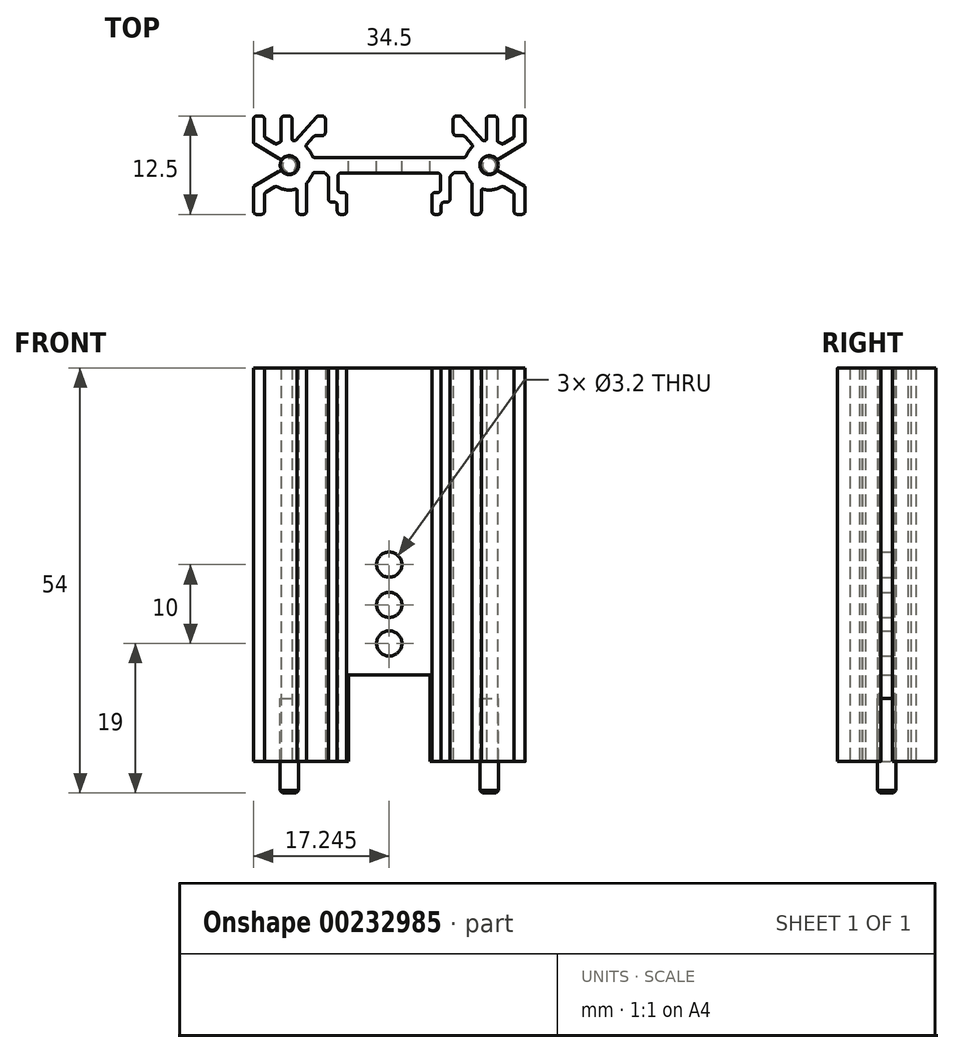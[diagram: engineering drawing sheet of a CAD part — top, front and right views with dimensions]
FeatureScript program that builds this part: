
annotation { "Feature Type Name" : "Feature", "Feature Type Description" : "" }
export const myFeature = defineFeature(function(context is Context, id is Id, definition is map)
    precondition{}
    {
        {
            var Q0;
            Q0=qCreatedBy(makeId("Top.planeOp"),FACE);
            var sketch = newSketch(context, id + "F0", { "sketchPlane" : qUnion([Q0])});
            skArc(sketch, "E0", {"start": v(-11.86, 14.65) * mm, "mid": v(-9.81, 15.5) * mm, "end": v(-11.85, 16.37) * mm});
            skPoint(sketch, "E0.first.point", {"position": v(-10.8, 16.69) * mm});
            skPoint(sketch, "E0.second.point", {"position": v(-9.82, 15.45) * mm});
            skPoint(sketch, "E0.third.point", {"position": v(-10.9, 14.31) * mm});
            skArc(sketch, "E1", {"start": v(-10.41, 18.6) * mm, "mid": v(-10.45, 18.6) * mm, "end": v(-10.48, 18.62) * mm});
            skPoint(sketch, "E1.first.point", {"position": v(-12.46, 18.31) * mm});
            skPoint(sketch, "E1.second.point", {"position": v(-10.9, 12.36) * mm});
            skPoint(sketch, "E1.third.point", {"position": v(-8.35, 17.19) * mm});
            skLineSegment(sketch, "E2", {"start": v(-12.05, 18.63) * mm, "end": v(-12.05, 21.36) * mm});
            skLineSegment(sketch, "E3", {"start": v(-10.65, 21.36) * mm, "end": v(-10.65, 18.81) * mm});
            skLineSegment(sketch, "E4", {"start": v(-10.22, 18.66) * mm, "end": v(-7.56, 21.63) * mm});
            skLineSegment(sketch, "E5", {"start": v(-11.05, 21.76) * mm, "end": v(-11.65, 21.76) * mm});
            skPoint(sketch, "E6.visualSharp", {"position": v(-12.05, 21.76) * mm});
            skArc(sketch, "E6.filletArc", {"start": v(-11.65, 21.76) * mm, "mid": v(-11.93, 21.64) * mm, "end": v(-12.05, 21.36) * mm});
            skPoint(sketch, "E7.visualSharp", {"position": v(-10.65, 21.76) * mm});
            skArc(sketch, "E7.filletArc", {"start": v(-10.65, 21.36) * mm, "mid": v(-10.77, 21.64) * mm, "end": v(-11.05, 21.76) * mm});
            skLineSegment(sketch, "E8", {"start": v(-12.8, 18.24) * mm, "end": v(-14.07, 19) * mm});
            skLineSegment(sketch, "E9", {"start": v(-14.16, 19.17) * mm, "end": v(-14.16, 21.36) * mm});
            skLineSegment(sketch, "E10", {"start": v(-14.56, 21.76) * mm, "end": v(-15.16, 21.76) * mm});
            skLineSegment(sketch, "E11", {"start": v(-15.56, 21.36) * mm, "end": v(-15.56, 18.5) * mm});
            skLineSegment(sketch, "E12", {"start": v(-15.37, 18.16) * mm, "end": v(-13.7, 17.15) * mm});
            skPoint(sketch, "E13.visualSharp", {"position": v(-15.56, 18.28) * mm});
            skArc(sketch, "E13.filletArc", {"start": v(-15.56, 18.5) * mm, "mid": v(-15.51, 18.3) * mm, "end": v(-15.37, 18.16) * mm});
            skPoint(sketch, "E14.visualSharp", {"position": v(-14.16, 19.06) * mm});
            skArc(sketch, "E14.filletArc", {"start": v(-14.16, 19.17) * mm, "mid": v(-14.14, 19.08) * mm, "end": v(-14.07, 19) * mm});
            skPoint(sketch, "E15.visualSharp", {"position": v(-14.16, 21.76) * mm});
            skArc(sketch, "E15.filletArc", {"start": v(-14.16, 21.36) * mm, "mid": v(-14.28, 21.64) * mm, "end": v(-14.56, 21.76) * mm});
            skPoint(sketch, "E16.visualSharp", {"position": v(-15.56, 21.76) * mm});
            skArc(sketch, "E16.filletArc", {"start": v(-15.16, 21.76) * mm, "mid": v(-15.45, 21.64) * mm, "end": v(-15.56, 21.36) * mm});
            skLineSegment(sketch, "E17", {"start": v(-7.92, 19.13) * mm, "end": v(-8.86, 18.08) * mm});
            skLineSegment(sketch, "E18", {"start": v(-13.72, 13.88) * mm, "end": v(-15.47, 12.83) * mm});
            skLineSegment(sketch, "E19", {"start": v(-15.56, 12.66) * mm, "end": v(-15.56, 9.66) * mm});
            skLineSegment(sketch, "E20", {"start": v(-15.16, 9.26) * mm, "end": v(-14.56, 9.26) * mm});
            skLineSegment(sketch, "E21", {"start": v(-14.16, 9.66) * mm, "end": v(-14.16, 11.74) * mm});
            skLineSegment(sketch, "E22", {"start": v(-13.97, 12.09) * mm, "end": v(-12.8, 12.79) * mm});
            skPoint(sketch, "E23.visualSharp", {"position": v(-14.16, 11.97) * mm});
            skArc(sketch, "E23.filletArc", {"start": v(-13.97, 12.09) * mm, "mid": v(-14.11, 11.94) * mm, "end": v(-14.16, 11.74) * mm});
            skPoint(sketch, "E24.visualSharp", {"position": v(-15.56, 12.77) * mm});
            skArc(sketch, "E24.filletArc", {"start": v(-15.47, 12.83) * mm, "mid": v(-15.54, 12.76) * mm, "end": v(-15.56, 12.66) * mm});
            skPoint(sketch, "E25.visualSharp", {"position": v(-14.16, 9.26) * mm});
            skArc(sketch, "E25.filletArc", {"start": v(-14.56, 9.26) * mm, "mid": v(-14.28, 9.38) * mm, "end": v(-14.16, 9.66) * mm});
            skPoint(sketch, "E26.visualSharp", {"position": v(-15.56, 9.26) * mm});
            skArc(sketch, "E26.filletArc", {"start": v(-15.56, 9.66) * mm, "mid": v(-15.45, 9.38) * mm, "end": v(-15.16, 9.26) * mm});
            skLineSegment(sketch, "E27", {"start": v(-10, 12.26) * mm, "end": v(-10, 9.66) * mm});
            skLineSegment(sketch, "E28", {"start": v(-9.6, 9.26) * mm, "end": v(-9.2, 9.26) * mm});
            skLineSegment(sketch, "E29", {"start": v(-8.8, 9.66) * mm, "end": v(-8.8, 13.18) * mm});
            skPoint(sketch, "E30.visualSharp", {"position": v(-10, 9.26) * mm});
            skArc(sketch, "E30.filletArc", {"start": v(-10, 9.66) * mm, "mid": v(-9.88, 9.38) * mm, "end": v(-9.6, 9.26) * mm});
            skPoint(sketch, "E31.visualSharp", {"position": v(-8.8, 9.26) * mm});
            skArc(sketch, "E31.filletArc", {"start": v(-9.2, 9.26) * mm, "mid": v(-8.92, 9.38) * mm, "end": v(-8.8, 9.66) * mm});
            skLineSegment(sketch, "E32", {"start": v(-7.87, 14.55) * mm, "end": v(-6.62, 14.55) * mm});
            skLineSegment(sketch, "E33", {"start": v(-6.48, 14.49) * mm, "end": v(-6.1, 14.1) * mm});
            skLineSegment(sketch, "E34", {"start": v(-6.04, 13.96) * mm, "end": v(-6.04, 11.22) * mm});
            skLineSegment(sketch, "E35", {"start": v(-5.64, 10.82) * mm, "end": v(-5.31, 10.82) * mm});
            skLineSegment(sketch, "E36", {"start": v(-4.91, 10.42) * mm, "end": v(-4.91, 9.66) * mm});
            skLineSegment(sketch, "E37", {"start": v(-4.51, 9.26) * mm, "end": v(-4.11, 9.26) * mm});
            skLineSegment(sketch, "E38", {"start": v(-3.71, 9.66) * mm, "end": v(-3.71, 11.62) * mm});
            skLineSegment(sketch, "E39", {"start": v(-4.11, 12.02) * mm, "end": v(-4.44, 12.02) * mm});
            skLineSegment(sketch, "E40", {"start": v(-4.84, 12.42) * mm, "end": v(-4.84, 14.1) * mm});
            skLineSegment(sketch, "E41", {"start": v(-4.44, 14.5) * mm, "end": v(1.69, 14.5) * mm});
            skLineSegment(sketch, "E42", {"start": v(1.69, 14.5) * mm, "end": v(1.69, 16.5) * mm, "construction": true});
            skLineSegment(sketch, "E43", {"start": v(1.69, 16.5) * mm, "end": v(-7.88, 16.5) * mm});
            skPoint(sketch, "E44.visualSharp", {"position": v(-4.84, 14.5) * mm});
            skArc(sketch, "E44.filletArc", {"start": v(-4.44, 14.5) * mm, "mid": v(-4.72, 14.39) * mm, "end": v(-4.84, 14.1) * mm});
            skPoint(sketch, "E45.visualSharp", {"position": v(-4.84, 12.02) * mm});
            skArc(sketch, "E45.filletArc", {"start": v(-4.84, 12.42) * mm, "mid": v(-4.72, 12.14) * mm, "end": v(-4.44, 12.02) * mm});
            skPoint(sketch, "E46.visualSharp", {"position": v(-3.71, 12.02) * mm});
            skArc(sketch, "E46.filletArc", {"start": v(-3.71, 11.62) * mm, "mid": v(-3.83, 11.9) * mm, "end": v(-4.11, 12.02) * mm});
            skPoint(sketch, "E47.visualSharp", {"position": v(-4.91, 10.82) * mm});
            skArc(sketch, "E47.filletArc", {"start": v(-4.91, 10.42) * mm, "mid": v(-5.03, 10.7) * mm, "end": v(-5.31, 10.82) * mm});
            skPoint(sketch, "E48.visualSharp", {"position": v(-6.04, 10.82) * mm});
            skArc(sketch, "E48.filletArc", {"start": v(-6.04, 11.22) * mm, "mid": v(-5.92, 10.94) * mm, "end": v(-5.64, 10.82) * mm});
            skPoint(sketch, "E49.visualSharp", {"position": v(-4.91, 9.26) * mm});
            skArc(sketch, "E49.filletArc", {"start": v(-4.91, 9.66) * mm, "mid": v(-4.8, 9.38) * mm, "end": v(-4.51, 9.26) * mm});
            skPoint(sketch, "E50.visualSharp", {"position": v(-3.71, 9.26) * mm});
            skArc(sketch, "E50.filletArc", {"start": v(-4.11, 9.26) * mm, "mid": v(-3.83, 9.38) * mm, "end": v(-3.71, 9.66) * mm});
            skLineSegment(sketch, "E51", {"start": v(-13.7, 17.15) * mm, "end": v(-12.33, 16.32) * mm});
            skLineSegment(sketch, "E52", {"start": v(-13.72, 13.88) * mm, "end": v(-12.34, 14.71) * mm});
            skArc(sketch, "E53.trimOffspring", {"start": v(-12.17, 18.44) * mm, "mid": v(-12.4, 18.34) * mm, "end": v(-12.6, 18.23) * mm});
            skArc(sketch, "E54.trimOffspring", {"start": v(-12.6, 12.79) * mm, "mid": v(-11.46, 12.39) * mm, "end": v(-10.25, 12.45) * mm});
            skArc(sketch, "E55.trimOffspring", {"start": v(-8.74, 13.32) * mm, "mid": v(-8.35, 13.83) * mm, "end": v(-8.06, 14.41) * mm});
            skArc(sketch, "E56.trimOffspring", {"start": v(-8.07, 16.63) * mm, "mid": v(-8.4, 17.26) * mm, "end": v(-8.85, 17.8) * mm});
            skPoint(sketch, "E57.visualSharp", {"position": v(-12.04, 16.14) * mm});
            skArc(sketch, "E57.filletArc", {"start": v(-12.33, 16.32) * mm, "mid": v(-12.08, 16.26) * mm, "end": v(-11.85, 16.37) * mm});
            skPoint(sketch, "E58.visualSharp", {"position": v(-12.04, 14.9) * mm});
            skArc(sketch, "E58.filletArc", {"start": v(-11.86, 14.65) * mm, "mid": v(-12.1, 14.77) * mm, "end": v(-12.34, 14.71) * mm});
            skPoint(sketch, "E59.visualSharp", {"position": v(-12.7, 18.17) * mm});
            skArc(sketch, "E59.filletArc", {"start": v(-12.8, 18.24) * mm, "mid": v(-12.7, 18.2) * mm, "end": v(-12.6, 18.23) * mm});
            skPoint(sketch, "E60.visualSharp", {"position": v(-12.05, 18.49) * mm});
            skArc(sketch, "E60.filletArc", {"start": v(-12.17, 18.44) * mm, "mid": v(-12.08, 18.51) * mm, "end": v(-12.05, 18.63) * mm});
            skPoint(sketch, "E61.visualSharp", {"position": v(-10.65, 18.64) * mm});
            skArc(sketch, "E61.filletArc", {"start": v(-10.65, 18.81) * mm, "mid": v(-10.6, 18.68) * mm, "end": v(-10.48, 18.62) * mm});
            skPoint(sketch, "E62.visualSharp", {"position": v(-10.3, 18.58) * mm});
            skArc(sketch, "E62.filletArc", {"start": v(-10.41, 18.6) * mm, "mid": v(-10.3, 18.6) * mm, "end": v(-10.22, 18.66) * mm});
            skPoint(sketch, "E63.visualSharp", {"position": v(-9, 17.93) * mm});
            skArc(sketch, "E63.filletArc", {"start": v(-8.86, 18.08) * mm, "mid": v(-8.92, 17.94) * mm, "end": v(-8.85, 17.8) * mm});
            skPoint(sketch, "E64.visualSharp", {"position": v(-8.02, 16.5) * mm});
            skArc(sketch, "E64.filletArc", {"start": v(-8.07, 16.63) * mm, "mid": v(-8, 16.54) * mm, "end": v(-7.88, 16.5) * mm});
            skPoint(sketch, "E65.visualSharp", {"position": v(-8.01, 14.55) * mm});
            skArc(sketch, "E65.filletArc", {"start": v(-7.87, 14.55) * mm, "mid": v(-7.99, 14.5) * mm, "end": v(-8.06, 14.41) * mm});
            skPoint(sketch, "E66.visualSharp", {"position": v(-8.8, 13.26) * mm});
            skArc(sketch, "E66.filletArc", {"start": v(-8.74, 13.32) * mm, "mid": v(-8.79, 13.26) * mm, "end": v(-8.8, 13.18) * mm});
            skPoint(sketch, "E67.visualSharp", {"position": v(-10, 12.52) * mm});
            skArc(sketch, "E67.filletArc", {"start": v(-10, 12.26) * mm, "mid": v(-10.08, 12.41) * mm, "end": v(-10.25, 12.45) * mm});
            skPoint(sketch, "E68.visualSharp", {"position": v(-12.7, 12.85) * mm});
            skArc(sketch, "E68.filletArc", {"start": v(-12.6, 12.79) * mm, "mid": v(-12.7, 12.81) * mm, "end": v(-12.8, 12.79) * mm});
            skPoint(sketch, "E69.visualSharp", {"position": v(-6.54, 14.55) * mm});
            skArc(sketch, "E69.filletArc", {"start": v(-6.48, 14.49) * mm, "mid": v(-6.54, 14.53) * mm, "end": v(-6.62, 14.55) * mm});
            skPoint(sketch, "E70.visualSharp", {"position": v(-6.04, 14.04) * mm});
            skArc(sketch, "E70.filletArc", {"start": v(-6.04, 13.96) * mm, "mid": v(-6.05, 14.03) * mm, "end": v(-6.1, 14.1) * mm});
            skArc(sketch, "E71.MirrorCS", {"start": v(16.17, 18.24) * mm, "mid": v(16.07, 18.2) * mm, "end": v(15.97, 18.23) * mm});
            skArc(sketch, "E72.MirrorCS", {"start": v(15.55, 18.44) * mm, "mid": v(15.45, 18.51) * mm, "end": v(15.42, 18.63) * mm});
            skArc(sketch, "E73.MirrorCS", {"start": v(15.55, 18.44) * mm, "mid": v(15.76, 18.34) * mm, "end": v(15.97, 18.23) * mm});
            skArc(sketch, "E74.MirrorCS", {"start": v(14.02, 18.81) * mm, "mid": v(13.97, 18.68) * mm, "end": v(13.85, 18.62) * mm});
            skArc(sketch, "E75.MirrorCS", {"start": v(13.78, 18.6) * mm, "mid": v(13.82, 18.6) * mm, "end": v(13.85, 18.62) * mm});
            skArc(sketch, "E76.MirrorCS", {"start": v(12.12, 13.32) * mm, "mid": v(12.16, 13.26) * mm, "end": v(12.17, 13.18) * mm});
            skLineSegment(sketch, "E77.MirrorCS", {"start": v(7.49, 12.02) * mm, "end": v(7.8, 12.02) * mm});
            skLineSegment(sketch, "E78.MirrorCS", {"start": v(9, 10.82) * mm, "end": v(8.69, 10.82) * mm});
            skArc(sketch, "E79.MirrorCS", {"start": v(9.4, 11.22) * mm, "mid": v(9.29, 10.94) * mm, "end": v(9, 10.82) * mm});
            skArc(sketch, "E80.MirrorCS", {"start": v(8.29, 10.42) * mm, "mid": v(8.4, 10.7) * mm, "end": v(8.69, 10.82) * mm});
            skArc(sketch, "E81.MirrorCS", {"start": v(7.09, 11.62) * mm, "mid": v(7.2, 11.9) * mm, "end": v(7.49, 12.02) * mm});
            skArc(sketch, "E82.MirrorCS", {"start": v(8.2, 12.42) * mm, "mid": v(8.09, 12.14) * mm, "end": v(7.8, 12.02) * mm});
            skLineSegment(sketch, "E83.MirrorCS", {"start": v(8.29, 10.42) * mm, "end": v(8.29, 9.66) * mm});
            skArc(sketch, "E84.MirrorCS", {"start": v(7.8, 14.5) * mm, "mid": v(8.09, 14.39) * mm, "end": v(8.2, 14.1) * mm});
            skLineSegment(sketch, "E85.MirrorCS", {"start": v(12.97, 9.26) * mm, "end": v(12.57, 9.26) * mm});
            skArc(sketch, "E86.MirrorCS", {"start": v(18.84, 12.83) * mm, "mid": v(18.9, 12.76) * mm, "end": v(18.94, 12.66) * mm});
            skArc(sketch, "E87.MirrorCS", {"start": v(18.94, 18.5) * mm, "mid": v(18.88, 18.3) * mm, "end": v(18.74, 18.16) * mm});
            skLineSegment(sketch, "E88.MirrorCS", {"start": v(8.2, 12.42) * mm, "end": v(8.2, 14.1) * mm});
            skLineSegment(sketch, "E89.MirrorCS", {"start": v(14.42, 21.76) * mm, "end": v(15.02, 21.76) * mm});
            skArc(sketch, "E90.MirrorCS", {"start": v(12.12, 13.32) * mm, "mid": v(11.72, 13.83) * mm, "end": v(11.43, 14.41) * mm});
            skArc(sketch, "E91.MirrorCS", {"start": v(9.85, 14.49) * mm, "mid": v(9.91, 14.53) * mm, "end": v(9.99, 14.55) * mm});
            skArc(sketch, "E92.MirrorCS", {"start": v(17.54, 19.17) * mm, "mid": v(17.5, 19.08) * mm, "end": v(17.44, 19) * mm});
            skArc(sketch, "E93.MirrorCS", {"start": v(15.97, 12.79) * mm, "mid": v(14.83, 12.39) * mm, "end": v(13.62, 12.45) * mm});
            skArc(sketch, "E94.MirrorCS", {"start": v(9.4, 13.96) * mm, "mid": v(9.42, 14.03) * mm, "end": v(9.46, 14.1) * mm});
            skArc(sketch, "E95.MirrorCS", {"start": v(14.02, 21.36) * mm, "mid": v(14.14, 21.64) * mm, "end": v(14.42, 21.76) * mm});
            skArc(sketch, "E96.MirrorCS", {"start": v(15.97, 12.79) * mm, "mid": v(16.08, 12.81) * mm, "end": v(16.18, 12.79) * mm});
            skArc(sketch, "E97.MirrorCS", {"start": v(15.02, 21.76) * mm, "mid": v(15.3, 21.64) * mm, "end": v(15.42, 21.36) * mm});
            skLineSegment(sketch, "E98.MirrorCS", {"start": v(16.17, 18.24) * mm, "end": v(17.44, 19) * mm});
            skLineSegment(sketch, "E99.MirrorCS", {"start": v(17.34, 12.09) * mm, "end": v(16.18, 12.79) * mm});
            skArc(sketch, "E100.MirrorCS", {"start": v(13.37, 12.26) * mm, "mid": v(13.45, 12.41) * mm, "end": v(13.62, 12.45) * mm});
            skArc(sketch, "E101.MirrorCS", {"start": v(11.24, 14.55) * mm, "mid": v(11.36, 14.5) * mm, "end": v(11.43, 14.41) * mm});
            skLineSegment(sketch, "E102.MirrorCS", {"start": v(9.85, 14.49) * mm, "end": v(9.46, 14.1) * mm});
            skArc(sketch, "E103.MirrorCS", {"start": v(8.29, 9.66) * mm, "mid": v(8.17, 9.38) * mm, "end": v(7.89, 9.26) * mm});
            skArc(sketch, "E104.MirrorCS", {"start": v(11.44, 16.63) * mm, "mid": v(11.37, 16.54) * mm, "end": v(11.25, 16.5) * mm});
            skLineSegment(sketch, "E105.MirrorCS", {"start": v(11.24, 14.55) * mm, "end": v(9.99, 14.55) * mm});
            skArc(sketch, "E106.MirrorCS", {"start": v(12.57, 9.26) * mm, "mid": v(12.29, 9.38) * mm, "end": v(12.17, 9.66) * mm});
            skArc(sketch, "E107.MirrorCS", {"start": v(13.37, 9.66) * mm, "mid": v(13.25, 9.38) * mm, "end": v(12.97, 9.26) * mm});
            skArc(sketch, "E108.MirrorCS", {"start": v(15.23, 14.65) * mm, "mid": v(15.46, 14.77) * mm, "end": v(15.71, 14.71) * mm});
            skArc(sketch, "E109.MirrorCS", {"start": v(17.34, 12.09) * mm, "mid": v(17.48, 11.94) * mm, "end": v(17.54, 11.74) * mm});
            skArc(sketch, "E110.MirrorCS", {"start": v(11.44, 16.63) * mm, "mid": v(11.77, 17.26) * mm, "end": v(12.22, 17.8) * mm});
            skArc(sketch, "E111.MirrorCS", {"start": v(15.7, 16.32) * mm, "mid": v(15.45, 16.26) * mm, "end": v(15.22, 16.37) * mm});
            skArc(sketch, "E112.MirrorCS", {"start": v(18.54, 21.76) * mm, "mid": v(18.82, 21.64) * mm, "end": v(18.94, 21.36) * mm});
            skLineSegment(sketch, "E113.MirrorCS", {"start": v(17.54, 9.66) * mm, "end": v(17.54, 11.74) * mm});
            skArc(sketch, "E114.MirrorCS", {"start": v(17.54, 21.36) * mm, "mid": v(17.65, 21.64) * mm, "end": v(17.94, 21.76) * mm});
            skLineSegment(sketch, "E115.MirrorCS", {"start": v(7.89, 9.26) * mm, "end": v(7.49, 9.26) * mm});
            skLineSegment(sketch, "E116.MirrorCS", {"start": v(18.54, 9.26) * mm, "end": v(17.94, 9.26) * mm});
            skLineSegment(sketch, "E117.MirrorCS", {"start": v(17.94, 21.76) * mm, "end": v(18.54, 21.76) * mm});
            skLineSegment(sketch, "E118.MirrorCS", {"start": v(17.54, 19.17) * mm, "end": v(17.54, 21.36) * mm});
            skLineSegment(sketch, "E119.MirrorCS", {"start": v(7.09, 9.66) * mm, "end": v(7.09, 11.62) * mm});
            skArc(sketch, "E120.MirrorCS", {"start": v(7.49, 9.26) * mm, "mid": v(7.2, 9.38) * mm, "end": v(7.09, 9.66) * mm});
            skArc(sketch, "E121.MirrorCS", {"start": v(18.94, 9.66) * mm, "mid": v(18.82, 9.38) * mm, "end": v(18.54, 9.26) * mm});
            skArc(sketch, "E122.MirrorCS", {"start": v(17.94, 9.26) * mm, "mid": v(17.65, 9.38) * mm, "end": v(17.54, 9.66) * mm});
            skArc(sketch, "E123.MirrorCS", {"start": v(15.23, 14.65) * mm, "mid": v(13.19, 15.5) * mm, "end": v(15.22, 16.37) * mm});
            skPoint(sketch, "E124.MirrorP", {"position": v(14.02, 18.64) * mm});
            skLineSegment(sketch, "E125.MirrorCS", {"start": v(17.08, 17.15) * mm, "end": v(15.7, 16.32) * mm});
            skLineSegment(sketch, "E126.MirrorCS", {"start": v(17.09, 13.88) * mm, "end": v(18.84, 12.83) * mm});
            skLineSegment(sketch, "E127.MirrorCS", {"start": v(9.4, 13.96) * mm, "end": v(9.4, 11.22) * mm});
            skLineSegment(sketch, "E128.MirrorCS", {"start": v(18.74, 18.16) * mm, "end": v(17.08, 17.15) * mm});
            skLineSegment(sketch, "E129.MirrorCS", {"start": v(17.09, 13.88) * mm, "end": v(15.71, 14.71) * mm});
            skPoint(sketch, "E130.MirrorP", {"position": v(14.27, 12.36) * mm});
            skLineSegment(sketch, "E131.MirrorCS", {"start": v(13.37, 12.26) * mm, "end": v(13.37, 9.66) * mm});
            skPoint(sketch, "E132.MirrorP", {"position": v(11.72, 17.19) * mm});
            skPoint(sketch, "E133.MirrorP", {"position": v(11.4, 16.5) * mm});
            skLineSegment(sketch, "E134.MirrorCS", {"start": v(18.94, 21.36) * mm, "end": v(18.94, 18.5) * mm});
            skLineSegment(sketch, "E135.MirrorCS", {"start": v(15.42, 18.63) * mm, "end": v(15.42, 21.36) * mm});
            skPoint(sketch, "E136.MirrorP", {"position": v(14.27, 14.31) * mm});
            skPoint(sketch, "E137.MirrorP", {"position": v(15.83, 18.31) * mm});
            skPoint(sketch, "E138.MirrorP", {"position": v(15.42, 18.49) * mm});
            skPoint(sketch, "E139.MirrorP", {"position": v(13.19, 15.45) * mm});
            skPoint(sketch, "E140.MirrorP", {"position": v(14.16, 16.69) * mm});
            skPoint(sketch, "E141.MirrorP", {"position": v(8.29, 10.82) * mm});
            skPoint(sketch, "E142.MirrorP", {"position": v(16.07, 18.17) * mm});
            skPoint(sketch, "E143.MirrorP", {"position": v(13.37, 12.52) * mm});
            skPoint(sketch, "E144.MirrorP", {"position": v(17.54, 19.06) * mm});
            skLineSegment(sketch, "E145.MirrorCS", {"start": v(18.94, 12.66) * mm, "end": v(18.94, 9.66) * mm});
            skPoint(sketch, "E146.MirrorP", {"position": v(7.09, 12.02) * mm});
            skPoint(sketch, "E147.MirrorP", {"position": v(17.54, 11.97) * mm});
            skPoint(sketch, "E148.MirrorP", {"position": v(12.17, 13.26) * mm});
            skPoint(sketch, "E149.MirrorP", {"position": v(15.41, 14.9) * mm});
            skPoint(sketch, "E150.MirrorP", {"position": v(8.2, 12.02) * mm});
            skPoint(sketch, "E151.MirrorP", {"position": v(15.4, 16.14) * mm});
            skPoint(sketch, "E152.MirrorP", {"position": v(11.38, 14.55) * mm});
            skLineSegment(sketch, "E153.MirrorCS", {"start": v(12.17, 9.66) * mm, "end": v(12.17, 13.18) * mm});
            skPoint(sketch, "E154.MirrorP", {"position": v(9.4, 10.82) * mm});
            skPoint(sketch, "E155.MirrorP", {"position": v(9.4, 14.04) * mm});
            skLineSegment(sketch, "E156.MirrorCS", {"start": v(14.02, 21.36) * mm, "end": v(14.02, 18.81) * mm});
            skPoint(sketch, "E157.MirrorP", {"position": v(12.17, 9.26) * mm});
            skLineSegment(sketch, "E158.MirrorCS", {"start": v(7.8, 14.5) * mm, "end": v(1.69, 14.5) * mm});
            skLineSegment(sketch, "E159.MirrorCS", {"start": v(1.69, 16.5) * mm, "end": v(11.25, 16.5) * mm});
            skPoint(sketch, "E160.MirrorP", {"position": v(8.2, 14.5) * mm});
            skPoint(sketch, "E161.MirrorP", {"position": v(15.42, 21.76) * mm});
            skPoint(sketch, "E162.MirrorP", {"position": v(8.29, 9.26) * mm});
            skPoint(sketch, "E163.MirrorP", {"position": v(18.94, 9.26) * mm});
            skPoint(sketch, "E164.MirrorP", {"position": v(18.94, 21.76) * mm});
            skPoint(sketch, "E165.MirrorP", {"position": v(18.94, 12.77) * mm});
            skPoint(sketch, "E166.MirrorP", {"position": v(18.94, 18.28) * mm});
            skPoint(sketch, "E167.MirrorP", {"position": v(14.02, 21.76) * mm});
            skPoint(sketch, "E168.MirrorP", {"position": v(9.9, 14.55) * mm});
            skPoint(sketch, "E169.MirrorP", {"position": v(16.08, 12.85) * mm});
            skPoint(sketch, "E170.MirrorP", {"position": v(17.54, 21.76) * mm});
            skPoint(sketch, "E171.MirrorP", {"position": v(7.09, 9.26) * mm});
            skPoint(sketch, "E172.MirrorP", {"position": v(13.37, 9.26) * mm});
            skPoint(sketch, "E173.MirrorP", {"position": v(17.54, 9.26) * mm});
            skLineSegment(sketch, "E174", {"start": v(-14.86, 21.76) * mm, "end": v(-8.24, 21.76) * mm, "construction": true});
            skPoint(sketch, "E174.endSnap0", {"position": v(-11.35, 21.76) * mm});
            skLineSegment(sketch, "E175", {"start": v(-7.26, 21.76) * mm, "end": v(-6.84, 21.76) * mm});
            skLineSegment(sketch, "E176", {"start": v(-6.44, 21.36) * mm, "end": v(-6.44, 19.66) * mm});
            skLineSegment(sketch, "E177", {"start": v(-6.84, 19.26) * mm, "end": v(-7.63, 19.26) * mm});
            skPoint(sketch, "E178.visualSharp", {"position": v(-7.44, 21.76) * mm});
            skArc(sketch, "E178.filletArc", {"start": v(-7.26, 21.76) * mm, "mid": v(-7.42, 21.72) * mm, "end": v(-7.56, 21.63) * mm});
            skPoint(sketch, "E179.visualSharp", {"position": v(-6.44, 21.76) * mm});
            skArc(sketch, "E179.filletArc", {"start": v(-6.44, 21.36) * mm, "mid": v(-6.55, 21.64) * mm, "end": v(-6.84, 21.76) * mm});
            skPoint(sketch, "E180.visualSharp", {"position": v(-6.44, 19.26) * mm});
            skArc(sketch, "E180.filletArc", {"start": v(-6.84, 19.26) * mm, "mid": v(-6.55, 19.38) * mm, "end": v(-6.44, 19.66) * mm});
            skPoint(sketch, "E181.visualSharp", {"position": v(-7.8, 19.26) * mm});
            skArc(sketch, "E181.filletArc", {"start": v(-7.63, 19.26) * mm, "mid": v(-7.79, 19.22) * mm, "end": v(-7.92, 19.13) * mm});
            skArc(sketch, "E182.MirrorCS", {"start": v(13.78, 18.6) * mm, "mid": v(13.68, 18.6) * mm, "end": v(13.6, 18.66) * mm});
            skArc(sketch, "E183.MirrorCS", {"start": v(12.23, 18.08) * mm, "mid": v(12.29, 17.94) * mm, "end": v(12.22, 17.8) * mm});
            skArc(sketch, "E184.MirrorCS", {"start": v(11, 19.26) * mm, "mid": v(11.16, 19.22) * mm, "end": v(11.3, 19.13) * mm});
            skArc(sketch, "E185.MirrorCS", {"start": v(10.63, 21.76) * mm, "mid": v(10.8, 21.72) * mm, "end": v(10.93, 21.63) * mm});
            skPoint(sketch, "E186.MirrorP", {"position": v(11.18, 19.26) * mm});
            skPoint(sketch, "E187.MirrorP", {"position": v(10.8, 21.76) * mm});
            skLineSegment(sketch, "E188.MirrorCS", {"start": v(9.8, 21.36) * mm, "end": v(9.8, 19.66) * mm});
            skLineSegment(sketch, "E189.MirrorCS", {"start": v(13.6, 18.66) * mm, "end": v(10.93, 21.63) * mm});
            skArc(sketch, "E190.MirrorCS", {"start": v(10.2, 19.26) * mm, "mid": v(9.93, 19.38) * mm, "end": v(9.8, 19.66) * mm});
            skPoint(sketch, "E191.MirrorP", {"position": v(9.8, 19.26) * mm});
            skArc(sketch, "E192.MirrorCS", {"start": v(9.8, 21.36) * mm, "mid": v(9.93, 21.64) * mm, "end": v(10.2, 21.76) * mm});
            skLineSegment(sketch, "E193.MirrorCS", {"start": v(10.2, 19.26) * mm, "end": v(11, 19.26) * mm});
            skPoint(sketch, "E194.MirrorP", {"position": v(9.8, 21.76) * mm});
            skLineSegment(sketch, "E195.MirrorCS", {"start": v(11.3, 19.13) * mm, "end": v(12.23, 18.08) * mm});
            skLineSegment(sketch, "E196.MirrorCS", {"start": v(10.63, 21.76) * mm, "end": v(10.2, 21.76) * mm});
            skSolve(sketch);
        }
        {
            var Q0;
            Q0 = qSketchRegion(id + "F0", true);
            extrude(context, id + "F1", {"entities" : qUnion([Q0]), "depth" : 50 * mm});
        }
        {
            var Q0;
            Q0=makeQuery(id+"F1.opExtrude","CAP_FACE",FACE,{"disambiguationData":[OSD([sQuery(id+"F0.wireOp",EDGE,"E0"),sQuery(id+"F0.wireOp",EDGE,"E1"),sQuery(id+"F0.wireOp",EDGE,"E2"),sQuery(id+"F0.wireOp",EDGE,"E3"),sQuery(id+"F0.wireOp",EDGE,"E4"),sQuery(id+"F0.wireOp",EDGE,"xrKfryI7-SMuP-rIyc-YWGD-kfCU0E0u5lao"),sQuery(id+"F0.wireOp",EDGE,"Sk6NL0oq-br1M-ovPf-d1jB-DepJBVRwD9Le"),sQuery(id+"F0.wireOp",EDGE,"E5"),sQuery(id+"F0.wireOp",EDGE,"E6.filletArc"),sQuery(id+"F0.wireOp",EDGE,"E7.filletArc"),sQuery(id+"F0.wireOp",EDGE,"E8"),sQuery(id+"F0.wireOp",EDGE,"E9"),sQuery(id+"F0.wireOp",EDGE,"E10"),sQuery(id+"F0.wireOp",EDGE,"E11"),sQuery(id+"F0.wireOp",EDGE,"E12"),sQuery(id+"F0.wireOp",EDGE,"E13.filletArc"),sQuery(id+"F0.wireOp",EDGE,"E14.filletArc"),sQuery(id+"F0.wireOp",EDGE,"E15.filletArc"),sQuery(id+"F0.wireOp",EDGE,"E16.filletArc"),sQuery(id+"F0.wireOp",EDGE,"9KWR2lmJ-Mqq0-4avW-B11Q-zaYOZBampOKE"),sQuery(id+"F0.wireOp",EDGE,"E17"),sQuery(id+"F0.wireOp",EDGE,"a7743309-fa18-45f4-a19c-e702701f491d.filletArc"),sQuery(id+"F0.wireOp",EDGE,"f29f7c9d-a5f2-4bce-bd93-7d0ead8df367.filletArc"),sQuery(id+"F0.wireOp",EDGE,"cfabb99c-02ee-45a6-a820-3355b5bed6c4.filletArc"),sQuery(id+"F0.wireOp",EDGE,"8cf2c7ae-949e-4d81-9e55-acf25f1c2067.filletArc"),sQuery(id+"F0.wireOp",EDGE,"E18"),sQuery(id+"F0.wireOp",EDGE,"E19"),sQuery(id+"F0.wireOp",EDGE,"E20"),sQuery(id+"F0.wireOp",EDGE,"E21"),sQuery(id+"F0.wireOp",EDGE,"E22"),sQuery(id+"F0.wireOp",EDGE,"E23.filletArc"),sQuery(id+"F0.wireOp",EDGE,"E24.filletArc"),sQuery(id+"F0.wireOp",EDGE,"E25.filletArc"),sQuery(id+"F0.wireOp",EDGE,"E26.filletArc"),sQuery(id+"F0.wireOp",EDGE,"E27"),sQuery(id+"F0.wireOp",EDGE,"E28"),sQuery(id+"F0.wireOp",EDGE,"E29"),sQuery(id+"F0.wireOp",EDGE,"E30.filletArc"),sQuery(id+"F0.wireOp",EDGE,"E31.filletArc"),sQuery(id+"F0.wireOp",EDGE,"E32"),sQuery(id+"F0.wireOp",EDGE,"E33"),sQuery(id+"F0.wireOp",EDGE,"E34"),sQuery(id+"F0.wireOp",EDGE,"E35"),sQuery(id+"F0.wireOp",EDGE,"E36"),sQuery(id+"F0.wireOp",EDGE,"E37"),sQuery(id+"F0.wireOp",EDGE,"E38"),sQuery(id+"F0.wireOp",EDGE,"E39"),sQuery(id+"F0.wireOp",EDGE,"E40"),sQuery(id+"F0.wireOp",EDGE,"E41"),sQuery(id+"F0.wireOp",EDGE,"E43"),sQuery(id+"F0.wireOp",EDGE,"E44.filletArc"),sQuery(id+"F0.wireOp",EDGE,"E45.filletArc"),sQuery(id+"F0.wireOp",EDGE,"E46.filletArc"),sQuery(id+"F0.wireOp",EDGE,"E47.filletArc"),sQuery(id+"F0.wireOp",EDGE,"E48.filletArc"),sQuery(id+"F0.wireOp",EDGE,"E49.filletArc"),sQuery(id+"F0.wireOp",EDGE,"E50.filletArc"),sQuery(id+"F0.wireOp",EDGE,"E51"),sQuery(id+"F0.wireOp",EDGE,"E52"),sQuery(id+"F0.wireOp",EDGE,"E53.trimOffspring"),sQuery(id+"F0.wireOp",EDGE,"E54.trimOffspring"),sQuery(id+"F0.wireOp",EDGE,"E55.trimOffspring"),sQuery(id+"F0.wireOp",EDGE,"E56.trimOffspring"),sQuery(id+"F0.wireOp",EDGE,"E57.filletArc"),sQuery(id+"F0.wireOp",EDGE,"E58.filletArc"),sQuery(id+"F0.wireOp",EDGE,"fb9b416a-2a19-4f91-a079-8bb963b366790.MirrorCS"),sQuery(id+"F0.wireOp",EDGE,"fb9b416a-2a19-4f91-a079-8bb963b366791.MirrorCS"),sQuery(id+"F0.wireOp",EDGE,"fb9b416a-2a19-4f91-a079-8bb963b366792.MirrorCS"),sQuery(id+"F0.wireOp",EDGE,"fb9b416a-2a19-4f91-a079-8bb963b366793.MirrorCS"),sQuery(id+"F0.wireOp",EDGE,"fb9b416a-2a19-4f91-a079-8bb963b366794.MirrorCS"),sQuery(id+"F0.wireOp",EDGE,"fb9b416a-2a19-4f91-a079-8bb963b366795.MirrorCS"),sQuery(id+"F0.wireOp",EDGE,"fb9b416a-2a19-4f91-a079-8bb963b366796.MirrorCS"),sQuery(id+"F0.wireOp",EDGE,"fb9b416a-2a19-4f91-a079-8bb963b366797.MirrorCS"),sQuery(id+"F0.wireOp",EDGE,"fb9b416a-2a19-4f91-a079-8bb963b366798.MirrorCS"),sQuery(id+"F0.wireOp",EDGE,"fb9b416a-2a19-4f91-a079-8bb963b366799.MirrorCS"),sQuery(id+"F0.wireOp",EDGE,"fb9b416a-2a19-4f91-a079-8bb963b3667910.MirrorCS"),sQuery(id+"F0.wireOp",EDGE,"fb9b416a-2a19-4f91-a079-8bb963b3667911.MirrorCS"),sQuery(id+"F0.wireOp",EDGE,"fb9b416a-2a19-4f91-a079-8bb963b3667912.MirrorCS"),sQuery(id+"F0.wireOp",EDGE,"fb9b416a-2a19-4f91-a079-8bb963b3667913.MirrorCS"),sQuery(id+"F0.wireOp",EDGE,"fb9b416a-2a19-4f91-a079-8bb963b3667914.MirrorCS"),sQuery(id+"F0.wireOp",EDGE,"fb9b416a-2a19-4f91-a079-8bb963b3667915.MirrorCS"),sQuery(id+"F0.wireOp",EDGE,"fb9b416a-2a19-4f91-a079-8bb963b3667916.MirrorCS"),sQuery(id+"F0.wireOp",EDGE,"fb9b416a-2a19-4f91-a079-8bb963b3667917.MirrorCS"),sQuery(id+"F0.wireOp",EDGE,"fb9b416a-2a19-4f91-a079-8bb963b3667918.MirrorCS"),sQuery(id+"F0.wireOp",EDGE,"fb9b416a-2a19-4f91-a079-8bb963b3667919.MirrorCS"),sQuery(id+"F0.wireOp",EDGE,"fb9b416a-2a19-4f91-a079-8bb963b3667920.MirrorCS"),sQuery(id+"F0.wireOp",EDGE,"fb9b416a-2a19-4f91-a079-8bb963b3667921.MirrorCS"),sQuery(id+"F0.wireOp",EDGE,"fb9b416a-2a19-4f91-a079-8bb963b3667922.MirrorCS"),sQuery(id+"F0.wireOp",EDGE,"fb9b416a-2a19-4f91-a079-8bb963b3667923.MirrorCS"),sQuery(id+"F0.wireOp",EDGE,"fb9b416a-2a19-4f91-a079-8bb963b3667924.MirrorCS"),sQuery(id+"F0.wireOp",EDGE,"fb9b416a-2a19-4f91-a079-8bb963b3667925.MirrorCS"),sQuery(id+"F0.wireOp",EDGE,"fb9b416a-2a19-4f91-a079-8bb963b3667926.MirrorCS"),sQuery(id+"F0.wireOp",EDGE,"fb9b416a-2a19-4f91-a079-8bb963b3667927.MirrorCS"),sQuery(id+"F0.wireOp",EDGE,"fb9b416a-2a19-4f91-a079-8bb963b3667928.MirrorCS"),sQuery(id+"F0.wireOp",EDGE,"fb9b416a-2a19-4f91-a079-8bb963b3667929.MirrorCS"),sQuery(id+"F0.wireOp",EDGE,"fb9b416a-2a19-4f91-a079-8bb963b3667930.MirrorCS"),sQuery(id+"F0.wireOp",EDGE,"fb9b416a-2a19-4f91-a079-8bb963b3667931.MirrorCS"),sQuery(id+"F0.wireOp",EDGE,"fb9b416a-2a19-4f91-a079-8bb963b3667932.MirrorCS"),sQuery(id+"F0.wireOp",EDGE,"fb9b416a-2a19-4f91-a079-8bb963b3667933.MirrorCS"),sQuery(id+"F0.wireOp",EDGE,"fb9b416a-2a19-4f91-a079-8bb963b3667934.MirrorCS"),sQuery(id+"F0.wireOp",EDGE,"fb9b416a-2a19-4f91-a079-8bb963b3667935.MirrorCS"),sQuery(id+"F0.wireOp",EDGE,"fb9b416a-2a19-4f91-a079-8bb963b3667936.MirrorCS"),sQuery(id+"F0.wireOp",EDGE,"fb9b416a-2a19-4f91-a079-8bb963b3667937.MirrorCS"),sQuery(id+"F0.wireOp",EDGE,"fb9b416a-2a19-4f91-a079-8bb963b3667938.MirrorCS"),sQuery(id+"F0.wireOp",EDGE,"fb9b416a-2a19-4f91-a079-8bb963b3667939.MirrorCS"),sQuery(id+"F0.wireOp",EDGE,"fb9b416a-2a19-4f91-a079-8bb963b3667940.MirrorCS"),sQuery(id+"F0.wireOp",EDGE,"fb9b416a-2a19-4f91-a079-8bb963b3667941.MirrorCS"),sQuery(id+"F0.wireOp",EDGE,"fb9b416a-2a19-4f91-a079-8bb963b3667942.MirrorCS"),sQuery(id+"F0.wireOp",EDGE,"fb9b416a-2a19-4f91-a079-8bb963b3667943.MirrorCS"),sQuery(id+"F0.wireOp",EDGE,"fb9b416a-2a19-4f91-a079-8bb963b3667944.MirrorCS"),sQuery(id+"F0.wireOp",EDGE,"fb9b416a-2a19-4f91-a079-8bb963b3667945.MirrorCS"),sQuery(id+"F0.wireOp",EDGE,"fb9b416a-2a19-4f91-a079-8bb963b3667946.MirrorCS"),sQuery(id+"F0.wireOp",EDGE,"fb9b416a-2a19-4f91-a079-8bb963b3667947.MirrorCS"),sQuery(id+"F0.wireOp",EDGE,"fb9b416a-2a19-4f91-a079-8bb963b3667948.MirrorCS"),sQuery(id+"F0.wireOp",EDGE,"fb9b416a-2a19-4f91-a079-8bb963b3667949.MirrorCS"),sQuery(id+"F0.wireOp",EDGE,"fb9b416a-2a19-4f91-a079-8bb963b3667950.MirrorCS"),sQuery(id+"F0.wireOp",EDGE,"fb9b416a-2a19-4f91-a079-8bb963b3667951.MirrorCS"),sQuery(id+"F0.wireOp",EDGE,"fb9b416a-2a19-4f91-a079-8bb963b3667952.MirrorCS"),sQuery(id+"F0.wireOp",EDGE,"fb9b416a-2a19-4f91-a079-8bb963b3667953.MirrorCS"),sQuery(id+"F0.wireOp",EDGE,"fb9b416a-2a19-4f91-a079-8bb963b3667958.MirrorCS"),sQuery(id+"F0.wireOp",EDGE,"fb9b416a-2a19-4f91-a079-8bb963b3667959.MirrorCS"),sQuery(id+"F0.wireOp",EDGE,"fb9b416a-2a19-4f91-a079-8bb963b3667960.MirrorCS"),sQuery(id+"F0.wireOp",EDGE,"fb9b416a-2a19-4f91-a079-8bb963b3667964.MirrorCS"),sQuery(id+"F0.wireOp",EDGE,"fb9b416a-2a19-4f91-a079-8bb963b3667965.MirrorCS"),sQuery(id+"F0.wireOp",EDGE,"fb9b416a-2a19-4f91-a079-8bb963b3667973.MirrorCS"),sQuery(id+"F0.wireOp",EDGE,"fb9b416a-2a19-4f91-a079-8bb963b3667978.MirrorCS"),sQuery(id+"F0.wireOp",EDGE,"fb9b416a-2a19-4f91-a079-8bb963b3667979.MirrorCS"),sQuery(id+"F0.wireOp",EDGE,"fb9b416a-2a19-4f91-a079-8bb963b3667987.MirrorCS"),sQuery(id+"F0.wireOp",EDGE,"fb9b416a-2a19-4f91-a079-8bb963b3667992.MirrorCS"),sQuery(id+"F0.wireOp",EDGE,"fb9b416a-2a19-4f91-a079-8bb963b3667993.MirrorCS")])],"isStart":true});
            var sketch = newSketch(context, id + "F2", { "sketchPlane" : qUnion([Q0])});
            skArc(sketch, "E197.0", {"start": v(-11.86, -14.65) * mm, "mid": v(-9.81, -15.5) * mm, "end": v(-11.85, -16.37) * mm, "construction": true});
            skArc(sketch, "E198", {"start": v(-11.86, -14.65) * mm, "mid": v(-12.21, -15.51) * mm, "end": v(-11.85, -16.37) * mm, "construction": true});
            skCircle(sketch, "E199", {"center": v(-11.01, -15.5) * mm, "radius": 1.15 * mm});
            skCircle(sketch, "E200", {"center": v(14.39, -15.5) * mm, "radius": 1.15 * mm});
            skArc(sketch, "E201.0", {"start": v(15.23, -14.65) * mm, "mid": v(13.19, -15.5) * mm, "end": v(15.22, -16.37) * mm, "construction": true});
            skArc(sketch, "E202", {"start": v(15.22, -16.37) * mm, "mid": v(15.59, -15.51) * mm, "end": v(15.23, -14.65) * mm, "construction": true});
            skSolve(sketch);
        }
        {
            var Q0;
            Q0 = qSketchRegion(id + "F2", true);
            extrude(context, id + "F3", {"entities" : qUnion([Q0]), "depth" : 4 * mm, "hasSecondDirection" : true, "secondDirectionOppositeDirection" : true, "secondDirectionDepth" : 8 * mm});
        }
        {
            var Q0;
            Q0=makeQuery(id+"F1.opExtrude","SWEPT_FACE",FACE,{"disambiguationData":[OSD([sQuery(id+"F0.wireOp",EDGE,"E43"),sQuery(id+"F0.wireOp",EDGE,"E159.MirrorCS")])]});
            var sketch = newSketch(context, id + "F4", { "sketchPlane" : qUnion([Q0])});
            skLineSegment(sketch, "E203.0", {"start": v(7.88, 0) * mm, "end": v(-11.25, 0) * mm, "construction": true});
            skLineSegment(sketch, "E203.1", {"start": v(7.88, 50) * mm, "end": v(-11.25, 50) * mm, "construction": true});
            skLineSegment(sketch, "E204", {"start": v(-1.69, 50) * mm, "end": v(-1.69, 0) * mm, "construction": true});
            skLineSegment(sketch, "E205.bottom", {"start": v(3.51, 11) * mm, "end": v(-6.89, 11) * mm});
            skLineSegment(sketch, "E205.top", {"start": v(3.51, -11) * mm, "end": v(-6.89, -11) * mm});
            skLineSegment(sketch, "E205.left", {"start": v(3.51, 11) * mm, "end": v(3.51, -11) * mm});
            skLineSegment(sketch, "E205.right", {"start": v(-6.89, 11) * mm, "end": v(-6.89, -11) * mm});
            skPoint(sketch, "E205.middle", {"position": v(-1.69, 0) * mm});
            skCircle(sketch, "E206", {"center": v(-1.69, 15) * mm, "radius": 1.6 * mm});
            skCircle(sketch, "E207", {"center": v(-1.69, 19.9) * mm, "radius": 1.6 * mm});
            skCircle(sketch, "E208", {"center": v(-1.69, 25) * mm, "radius": 1.6 * mm});
            skSolve(sketch);
        }
        {
            var Q0;
            Q0 = qSketchRegion(id + "F4", true);
            extrude(context, id + "F5", {"entities" : qUnion([Q0]), "operationType" : NewBodyOperationType.REMOVE, "endBound" : BoundingType.THROUGH_ALL, "oppositeDirection" : true, "depth" : 25 * mm});
        }
        {
            var Q0;
            Q0=makeQuery(id+"F3.opExtrude","CAP_EDGE",EDGE,{"disambiguationData":[OSD([sQuery(id+"F2.wireOp",EDGE,"E200")])],"isStart":false});
            var Q1;
            Q1=makeQuery(id+"F3.opExtrude","CAP_EDGE",EDGE,{"disambiguationData":[OSD([sQuery(id+"F2.wireOp",EDGE,"E199")])],"isStart":false});
            chamfer(context, id + "F6", {"entities" : qUnion([Q0, Q1]), "width" : 0.3 * mm, "tangentPropagation" : true});
        }
    });
